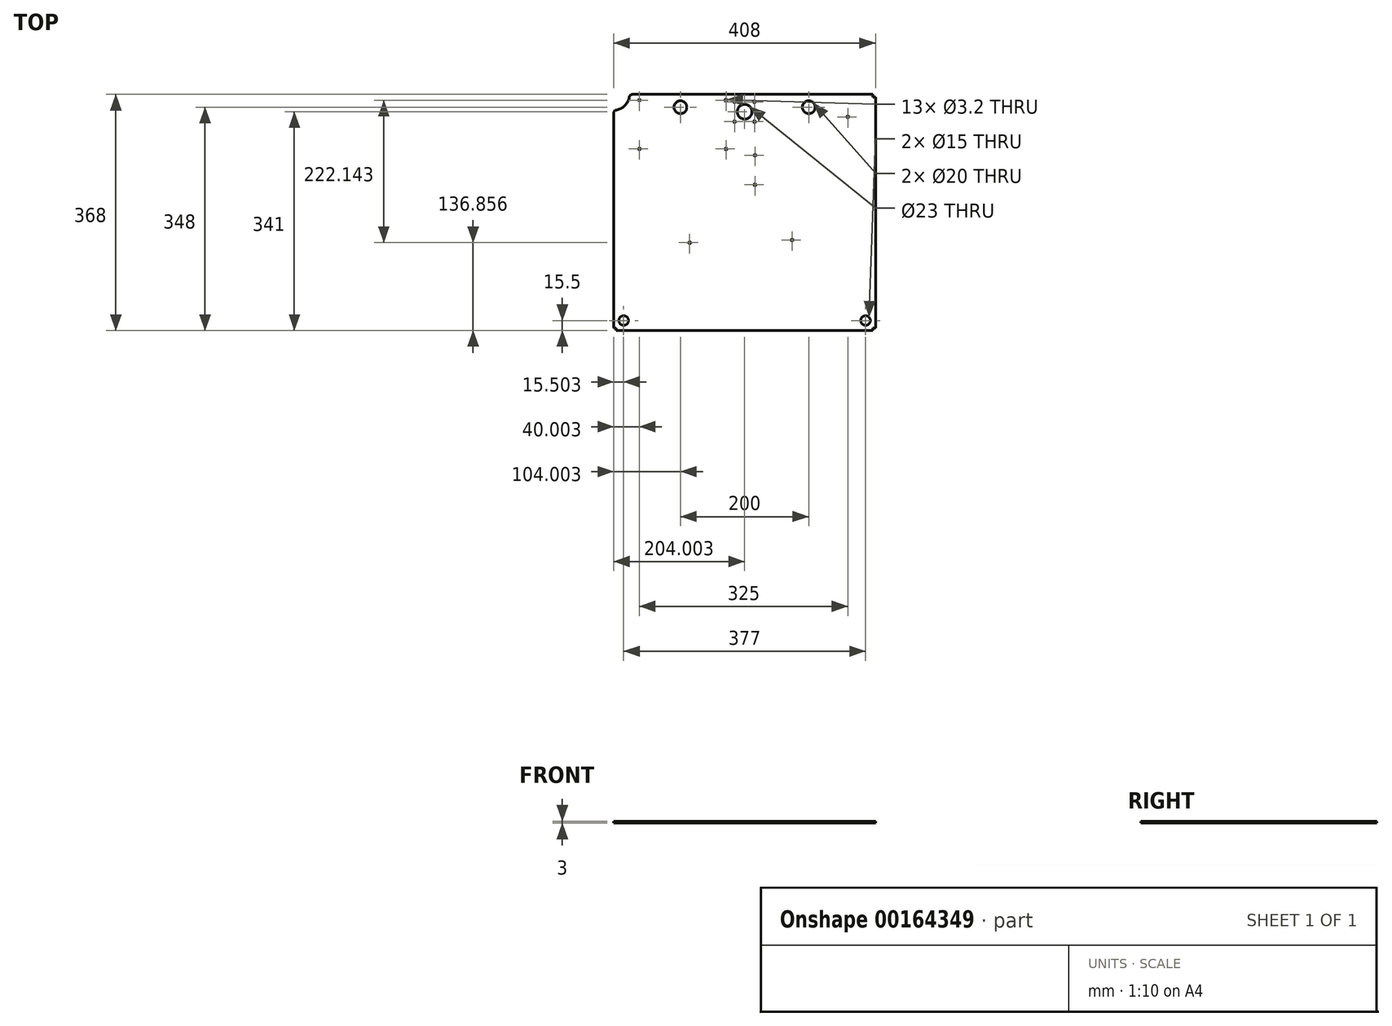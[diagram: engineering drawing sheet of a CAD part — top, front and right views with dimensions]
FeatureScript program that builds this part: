
annotation { "Feature Type Name" : "Feature", "Feature Type Description" : "" }
export const myFeature = defineFeature(function(context is Context, id is Id, definition is map)
    precondition{}
    {
        {
            var Q0;
            Q0=qCreatedBy(makeId("Top.planeOp"),FACE);
            var sketch = newSketch(context, id + "F0", { "sketchPlane" : qUnion([Q0])});
            skLineSegment(sketch, "E0.bottom", {"start": v(-284.09, 364.84) * mm, "end": v(90.72, 364.84) * mm});
            skLineSegment(sketch, "E0.top", {"start": v(-309.28, -3.16) * mm, "end": v(90.72, -3.16) * mm});
            skLineSegment(sketch, "E0.left", {"start": v(-313.28, 335.68) * mm, "end": v(-313.28, 0.84) * mm});
            skLineSegment(sketch, "E0.right", {"start": v(94.72, 360.84) * mm, "end": v(94.72, 0.84) * mm});
            skLineSegment(sketch, "E1", {"start": v(90.72, 364.84) * mm, "end": v(90.72, 360.84) * mm});
            skLineSegment(sketch, "E2", {"start": v(90.72, 360.84) * mm, "end": v(94.72, 360.84) * mm});
            skLineSegment(sketch, "E3", {"start": v(94.72, 0.84) * mm, "end": v(90.72, 0.84) * mm});
            skLineSegment(sketch, "E4", {"start": v(90.72, 0.84) * mm, "end": v(90.72, -3.16) * mm});
            skLineSegment(sketch, "E5", {"start": v(-313.28, 0.84) * mm, "end": v(-309.28, 0.84) * mm});
            skLineSegment(sketch, "E6", {"start": v(-309.28, 0.84) * mm, "end": v(-309.28, -3.16) * mm});
            skPoint(sketch, "E7.orphan", {"position": v(94.72, 364.84) * mm});
            skArc(sketch, "E8", {"start": v(-309.13, 340.6) * mm, "mid": v(-295.89, 347.46) * mm, "end": v(-289.02, 360.7) * mm});
            skPoint(sketch, "E9.start.orphan", {"position": v(-309.28, 360.84) * mm});
            skPoint(sketch, "E10.visualSharp", {"position": v(-288.65, 364.84) * mm});
            skArc(sketch, "E10.filletArc", {"start": v(-284.09, 364.84) * mm, "mid": v(-287.3, 363.67) * mm, "end": v(-289.02, 360.7) * mm});
            skPoint(sketch, "E11.visualSharp", {"position": v(-313.28, 340.25) * mm});
            skArc(sketch, "E11.filletArc", {"start": v(-309.13, 340.6) * mm, "mid": v(-312.1, 338.9) * mm, "end": v(-313.28, 335.68) * mm});
            skLineSegment(sketch, "E12", {"start": v(-326.8, 180.84) * mm, "end": v(113.22, 180.84) * mm, "construction": true});
            skLineSegment(sketch, "E13", {"start": v(-109.28, 377.2) * mm, "end": v(-109.28, -21.77) * mm, "construction": true});
            skCircle(sketch, "E14", {"center": v(-109.28, 337.84) * mm, "radius": 11.5 * mm});
            skCircle(sketch, "E15", {"center": v(-93.78, 353.34) * mm, "radius": 1.6 * mm});
            skCircle(sketch, "E16", {"center": v(-93.78, 322.34) * mm, "radius": 1.6 * mm});
            skCircle(sketch, "E17", {"center": v(-124.78, 322.34) * mm, "radius": 1.6 * mm});
            skCircle(sketch, "E18", {"center": v(-124.78, 353.34) * mm, "radius": 1.6 * mm});
            skCircle(sketch, "E19", {"center": v(-209.28, 344.84) * mm, "radius": 10 * mm});
            skCircle(sketch, "E20", {"center": v(-9.28, 344.84) * mm, "radius": 10 * mm});
            skCircle(sketch, "E21", {"center": v(-297.78, 12.34) * mm, "radius": 7.5 * mm});
            skCircle(sketch, "E22", {"center": v(79.22, 12.34) * mm, "radius": 7.5 * mm});
            skLineSegment(sketch, "E23.bottom", {"start": v(-273.28, 355.84) * mm, "end": v(-138.28, 355.84) * mm, "construction": true});
            skLineSegment(sketch, "E23.top", {"start": v(-273.28, 279.84) * mm, "end": v(-138.28, 279.84) * mm, "construction": true});
            skLineSegment(sketch, "E23.left", {"start": v(-273.28, 355.84) * mm, "end": v(-273.28, 279.84) * mm, "construction": true});
            skLineSegment(sketch, "E23.right", {"start": v(-138.28, 355.84) * mm, "end": v(-138.28, 279.84) * mm, "construction": true});
            skCircle(sketch, "E24", {"center": v(-273.28, 355.84) * mm, "radius": 1.6 * mm});
            skCircle(sketch, "E25", {"center": v(-273.28, 279.84) * mm, "radius": 1.6 * mm});
            skCircle(sketch, "E26", {"center": v(-138.28, 279.84) * mm, "radius": 1.6 * mm});
            skCircle(sketch, "E27", {"center": v(-138.28, 355.84) * mm, "radius": 1.6 * mm});
            skLineSegment(sketch, "E28.bottom", {"start": v(-35.28, 329.84) * mm, "end": v(51.72, 329.84) * mm, "construction": true});
            skLineSegment(sketch, "E28.top", {"start": v(-35.28, 137.84) * mm, "end": v(51.72, 137.84) * mm, "construction": true});
            skLineSegment(sketch, "E28.left", {"start": v(-35.28, 329.84) * mm, "end": v(-35.28, 137.84) * mm, "construction": true});
            skLineSegment(sketch, "E28.right", {"start": v(51.72, 329.84) * mm, "end": v(51.72, 137.84) * mm, "construction": true});
            skCircle(sketch, "E29", {"center": v(51.72, 329.84) * mm, "radius": 1.6 * mm});
            skCircle(sketch, "E30", {"center": v(-35.28, 137.84) * mm, "radius": 1.6 * mm});
            skLineSegment(sketch, "E31.bottom", {"start": v(-115.57, 276.38) * mm, "end": v(-70.57, 276.38) * mm, "construction": true});
            skLineSegment(sketch, "E31.top", {"start": v(-115.57, 214.38) * mm, "end": v(-70.57, 214.38) * mm, "construction": true});
            skLineSegment(sketch, "E31.left", {"start": v(-115.57, 276.38) * mm, "end": v(-115.57, 214.38) * mm, "construction": true});
            skLineSegment(sketch, "E31.right", {"start": v(-70.57, 276.38) * mm, "end": v(-70.57, 214.38) * mm, "construction": true});
            skLineSegment(sketch, "E32", {"start": v(-93.07, 276.38) * mm, "end": v(-93.07, 214.38) * mm, "construction": true});
            skCircle(sketch, "E33", {"center": v(-93.07, 269.88) * mm, "radius": 1.6 * mm});
            skCircle(sketch, "E34", {"center": v(-93.07, 223.88) * mm, "radius": 1.6 * mm});
            skCircle(sketch, "E35", {"center": v(-194.94, 133.7) * mm, "radius": 1.6 * mm});
            skSolve(sketch);
        }
        {
            var Q0;
            Q0 = qSketchRegion(id + "F0", true);
            extrude(context, id + "F1", {"entities" : qUnion([Q0]), "depth" : 3 * mm});
        }
    });
